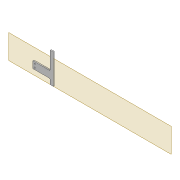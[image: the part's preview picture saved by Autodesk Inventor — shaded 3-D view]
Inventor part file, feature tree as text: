
AUTODESK INVENTOR PART (.ipt)
format: ipt  version: 2022 (Build 260153000, 153)  size: 516,608 bytes
history: native  units: mm
features: sketch x9, projected_geometry x9, extrude x8, fillet x2, shell x1, plane x1, chamfer x1
ambient origin geometry x8: Origin, YZ Plane, XZ Plane, XY Plane, X Axis, Y Axis, Z Axis, Center Point
bodies: Solid1 (feature_tree)
feature tree (31):
  extrude  "Extrusion1"  Depth=2.0mm
  shell  "Shell1"  Thickness=2.0mm
  extrude  "Extrusion8"  Depth=2.0mm
  extrude  "Extrusion3"  Depth=10.0mm TaperAngle=0.0deg
  extrude  "Extrusion4"  Depth=2.0mm
  fillet  "Fillet1"  Radius=80.0mm
  sketch  "Sketch10"  dims[d22=2.0mm d23=0.0mm d31=2.0mm d62=80.0mm]
  extrude  "Extrusion5"  Depth=2.0mm TaperAngle=0.0deg
  plane  "Work Plane2"
  extrude  "Extrusion10"  Depth=12.0mm
  fillet  "Fillet2"  Radius=5.0mm
  extrude  "Extrusion11"  Depth=12.0mm
  chamfer  "Chamfer1"  Distance=5.0mm
  extrude  "Extrusion13"  Depth=10.0mm TaperAngle=0.0deg
  sketch  "Sketch31"  dims[d75=30.0mm]
  sketch  "Sketch32"  dims[d76=3.05mm d77=5.0mm d78=10.0mm d79=0.0mm d80=2.0mm d81=100.0mm d82=20.0mm d83=1.6mm d84=1.6mm d85=2.5mm d86=2.5mm d87=0.5mm d88=10.0mm d89=0.0mm d92=10.0mm d93=10.0mm d94=3.0mm d95=2.0mm d96=45.0deg d98=1.0mm d99=1.0mm d100=1.0mm d101=1.0mm d102=1.0mm d103=1.0mm d104=10.0mm d105=0.0mm]
  sketch  "Sketch3"  dims[d0=2.0mm d1=0.0mm d2=4.0mm d7=2.0mm]
  sketch  "Sketch8"  dims[d8=2.0mm d9=5.9mm]
  sketch  "Sketch9"  dims[d13=10.0mm d14=0.0mm d16=10.0mm d17=0.0mm]
  projected_geometry  "Projected Loop4"
  projected_geometry  "Projected Loop10"
  sketch  "Sketch24"  dims[d63=6.0mm d64=2.0mm d65=0.0mm]
  projected_geometry  "Projected Loop11"
  projected_geometry  "Projected Loop12"
  projected_geometry  "Projected Loop13"
  sketch  "Sketch28"  dims[d66=3.0mm d67=12.0mm d68=5.0mm]
  projected_geometry  "Projected Loop14"
  sketch  "Sketch30"  dims[d69=5.0mm d74=12.0mm]
  projected_geometry  "Project Cut Edges1"
  projected_geometry  "Project Cut Edges2"
  projected_geometry  "Project Cut Edges3"
